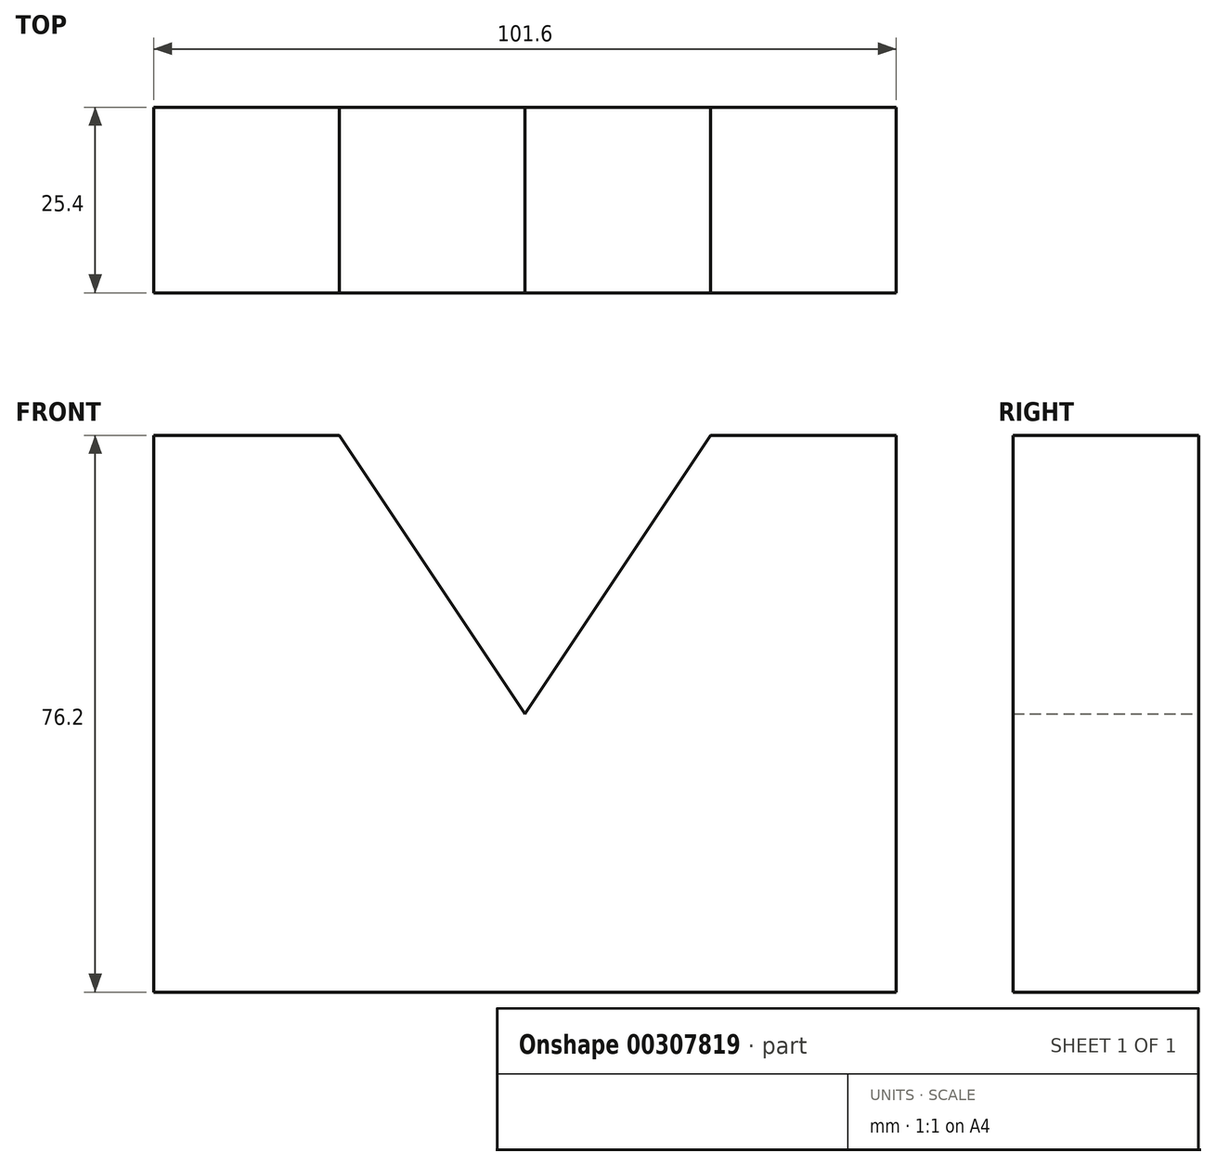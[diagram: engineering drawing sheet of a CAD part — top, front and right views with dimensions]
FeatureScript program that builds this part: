
annotation { "Feature Type Name" : "Feature", "Feature Type Description" : "" }
export const myFeature = defineFeature(function(context is Context, id is Id, definition is map)
    precondition{}
    {
        {
            var Q0;
            Q0=qCreatedBy(makeId("Front.planeOp"),FACE);
            var sketch = newSketch(context, id + "F0", { "sketchPlane" : qUnion([Q0])});
            skLineSegment(sketch, "E0", {"start": v(-45.05, -52.28) * mm, "end": v(56.55, -52.28) * mm});
            skLineSegment(sketch, "E1", {"start": v(56.55, -52.28) * mm, "end": v(56.55, 23.92) * mm});
            skLineSegment(sketch, "E2", {"start": v(-45.05, -52.28) * mm, "end": v(-45.05, 23.92) * mm});
            skLineSegment(sketch, "E3", {"start": v(-45.05, 23.92) * mm, "end": v(-19.65, 23.92) * mm});
            skLineSegment(sketch, "E4", {"start": v(56.55, 23.92) * mm, "end": v(31.15, 23.92) * mm});
            skLineSegment(sketch, "E5", {"start": v(5.75, -14.18) * mm, "end": v(-19.65, 23.92) * mm});
            skLineSegment(sketch, "E6", {"start": v(5.75, -14.18) * mm, "end": v(31.15, 23.92) * mm});
            skSolve(sketch);
        }
        {
            var Q0;
            Q0=makeQuery(id+"F0.imprint","IMPRINT",FACE,{"disambiguationData":[TD([[makeQuery(id+"F0.imprint","IMPRINT",EDGE,{"derivedFrom":sQuery(id+"F0.wireOp",EDGE,"E0")}),1.0]])]});
            extrude(context, id + "F1", {"entities" : qUnion([Q0]), "depth" : 25.4 * mm});
        }
    });
